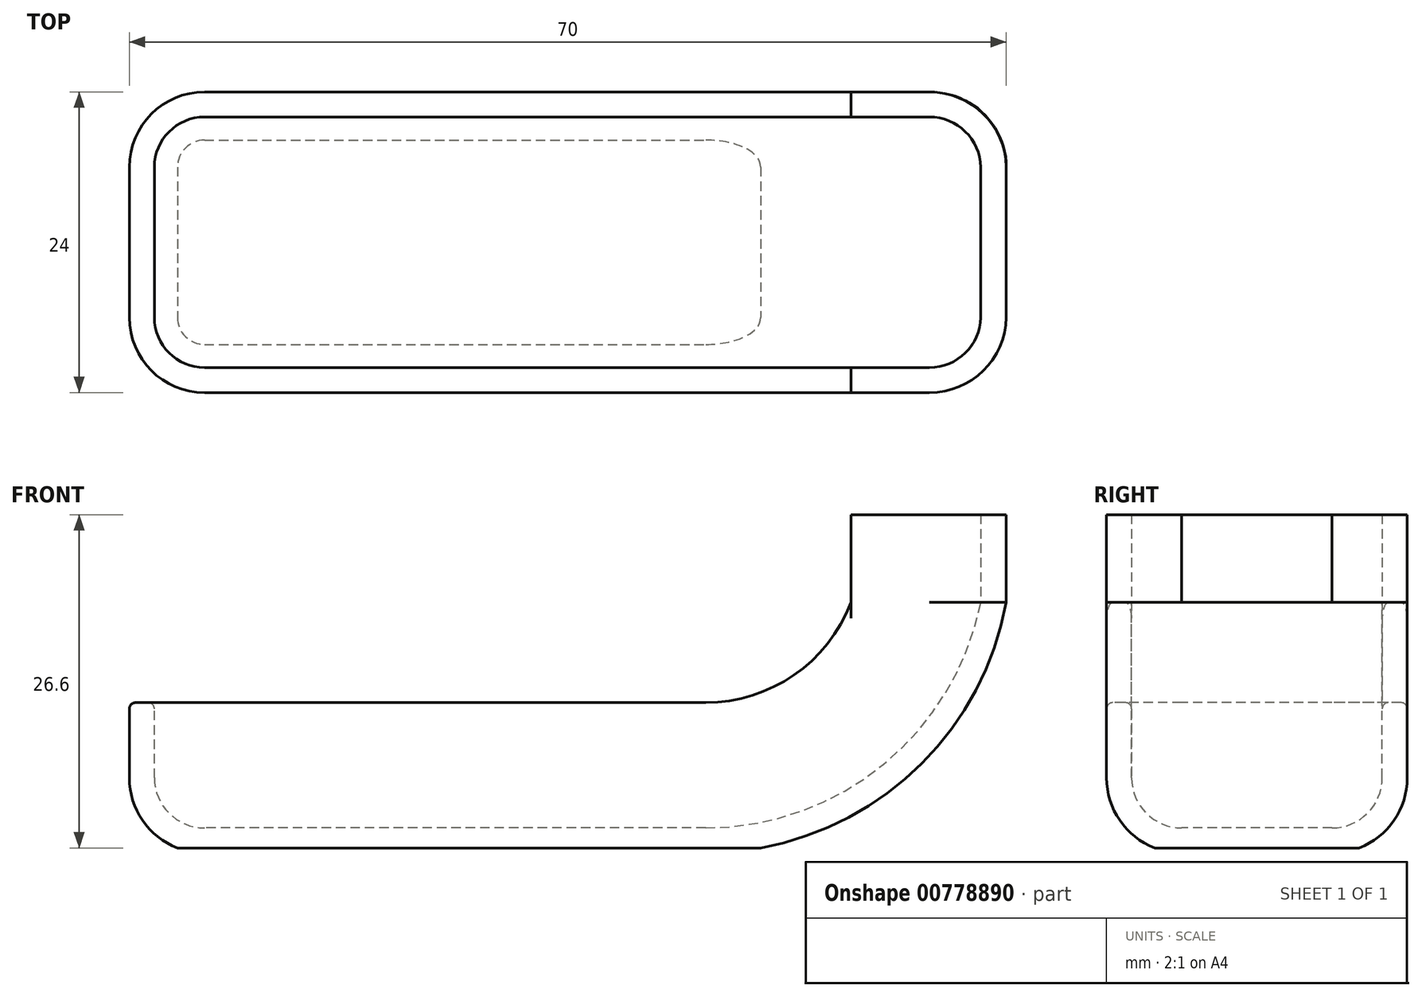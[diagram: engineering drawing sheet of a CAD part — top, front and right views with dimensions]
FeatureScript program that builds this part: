
annotation { "Feature Type Name" : "Feature", "Feature Type Description" : "" }
export const myFeature = defineFeature(function(context is Context, id is Id, definition is map)
    precondition{}
    {
        {
            var Q0;
            Q0=qCreatedBy(makeId("Front.planeOp"),FACE);
            var sketch = newSketch(context, id + "F0", { "sketchPlane" : qUnion([Q0])});
            skLineSegment(sketch, "E0", {"start": v(46, -24.4) * mm, "end": v(0, -24.4) * mm});
            skArc(sketch, "E1", {"start": v(46, -24.4) * mm, "mid": v(61.62, -18.74) * mm, "end": v(70, -4.4) * mm});
            skSolve(sketch);
        }
        {
            var Q0;
            Q0=qCreatedBy(makeId("Right.planeOp"),FACE);
            var sketch = newSketch(context, id + "F1", { "sketchPlane" : qUnion([Q0])});
            skArc(sketch, "E2", {"start": v(6, -24.4) * mm, "mid": v(10.24, -22.64) * mm, "end": v(12, -18.4) * mm});
            skArc(sketch, "E3", {"start": v(-12, -18.4) * mm, "mid": v(-10.24, -22.64) * mm, "end": v(-6, -24.4) * mm});
            skLineSegment(sketch, "E4", {"start": v(6, -24.4) * mm, "end": v(-6, -24.4) * mm});
            skLineSegment(sketch, "E5", {"start": v(12, -18.4) * mm, "end": v(12, -12.4) * mm});
            skLineSegment(sketch, "E6", {"start": v(12, -12.4) * mm, "end": v(-12, -12.4) * mm});
            skLineSegment(sketch, "E7", {"start": v(-12, -12.4) * mm, "end": v(-12, -18.4) * mm});
            skSolve(sketch);
        }
        {
            var Q0;
            Q0 = qSketchRegion(id + "F1", true);
            var Q1;
            Q1 = qConstructionFilter(qBodyType(qCreatedBy(id + "F0" ,EDGE), BodyType.WIRE), ConstructionObject.NO);
            sweep(context, id + "F2", {"profiles" : qUnion([Q0]), "path" : qUnion([Q1])});
        }
        {
            var Q0;
            Q0=makeQuery(id+"F2.opSweep","CAP_EDGE",EDGE,{"disambiguationData":[OSD([sQuery(id+"F0.wireOp",VERTEX,"E0.end"),sQuery(id+"F1.wireOp",EDGE,"E7")])],"isStart":true});
            fillet(context, id + "F3", {"entities" : qUnion([Q0]), "radius" : 6 * mm, "tangentPropagation" : true, "allowEdgeOverflow" : false});
        }
        {
            var Q0;
            Q0=makeQuery(id+"F2.opSweep","SWEPT_FACE",FACE,{"disambiguationData":[OSD([sQuery(id+"F0.wireOp",EDGE,"E0"),sQuery(id+"F1.wireOp",EDGE,"E6")])]});
            var Q1;
            Q1=makeQuery(id+"F2.opSweep","SWEPT_FACE",FACE,{"disambiguationData":[OSD([sQuery(id+"F0.wireOp",EDGE,"E1"),sQuery(id+"F1.wireOp",EDGE,"E6")])]});
            var Q2;
            Q2=makeQuery(id+"F2.opSweep","CAP_FACE",FACE,{"disambiguationData":[OSD([sQuery(id+"F0.wireOp",VERTEX,"E1.end"),sQuery(id+"F1.wireOp",EDGE,"E2"),sQuery(id+"F1.wireOp",EDGE,"E3"),sQuery(id+"F1.wireOp",EDGE,"E4"),sQuery(id+"F1.wireOp",EDGE,"E5"),sQuery(id+"F1.wireOp",EDGE,"E6"),sQuery(id+"F1.wireOp",EDGE,"E7")])],"isStart":false});
            shell(context, id + "F4", {"entities" : qUnion([Q0, Q1, Q2]), "thickness" : 2 * mm});
        }
        {
            var Q0;
            Q0=qCreatedBy(makeId("Top.planeOp"),FACE);
            var Q1;
            Q1=makeQuery(id+"F2.opSweep","CAP_VERTEX",VERTEX,{"disambiguationData":[OSD([sQuery(id+"F0.wireOp",EDGE,"E1"),sQuery(id+"F1.wireOp",EDGE,"E3"),sQuery(id+"F1.wireOp",EDGE,"E4")])],"isStart":false});
            cPlane(context, id + "F5", {"entities" : qUnion([Q0, Q1]), "cplaneType" : CPlaneType.PLANE_POINT, "offset" : 4 * mm, "oppositeDirection" : true, "width" : 150 * mm, "height" : 150 * mm});
        }
        {
            var Q0;
            Q0=qCreatedBy(id+"F5.planeOp",FACE);
            var sketch = newSketch(context, id + "F6", { "sketchPlane" : qUnion([Q0])});
            skLineSegment(sketch, "E8.bottom", {"start": v(34.96, 35.18) * mm, "end": v(78.53, 35.18) * mm});
            skLineSegment(sketch, "E8.top", {"start": v(34.96, -36.07) * mm, "end": v(78.53, -36.07) * mm});
            skLineSegment(sketch, "E8.left", {"start": v(34.96, 35.18) * mm, "end": v(34.96, -36.07) * mm});
            skLineSegment(sketch, "E8.right", {"start": v(78.53, 35.18) * mm, "end": v(78.53, -36.07) * mm});
            skSolve(sketch);
        }
        {
            var Q0;
            Q0 = qSketchRegion(id + "F6", true);
            extrude(context, id + "F7", {"entities" : qUnion([Q0]), "operationType" : NewBodyOperationType.REMOVE, "depth" : 25.2 * mm, "offsetDistance" : 25 * mm});
        }
        {
            var Q0;
            Q0=makeQuery(id+"F7.boolean.opBoolean","COPY",FACE,{"derivedFrom":makeQuery(id+"F7.opExtrude","CAP_FACE",FACE,{"disambiguationData":[OSD([sQuery(id+"F6.wireOp",EDGE,"E8.bottom"),sQuery(id+"F6.wireOp",EDGE,"E8.top"),sQuery(id+"F6.wireOp",EDGE,"E8.left"),sQuery(id+"F6.wireOp",EDGE,"E8.right")])],"isStart":true})});
            var sketch = newSketch(context, id + "F8", { "sketchPlane" : qUnion([Q0])});
            skLineSegment(sketch, "E9", {"start": v(57.6, 12) * mm, "end": v(57.6, 10) * mm});
            skLineSegment(sketch, "E10", {"start": v(57.6, 10) * mm, "end": v(63.87, 10) * mm});
            skLineSegment(sketch, "E11", {"start": v(57.6, -10) * mm, "end": v(63.87, -10) * mm});
            skLineSegment(sketch, "E12", {"start": v(57.6, -10) * mm, "end": v(57.6, -12) * mm});
            skLineSegment(sketch, "E13", {"start": v(57.6, -12) * mm, "end": v(63.87, -12) * mm});
            skLineSegment(sketch, "E14", {"start": v(67.96, -6) * mm, "end": v(67.96, 6) * mm});
            skLineSegment(sketch, "E15", {"start": v(70, 6) * mm, "end": v(70, -6) * mm});
            skLineSegment(sketch, "E16", {"start": v(57.6, 12) * mm, "end": v(63.87, 12) * mm});
            skArc(sketch, "E17", {"start": v(67.96, 6) * mm, "mid": v(66.73, 8.83) * mm, "end": v(63.87, 10) * mm});
            skArc(sketch, "E18", {"start": v(70, 6) * mm, "mid": v(68.16, 10.25) * mm, "end": v(63.87, 12) * mm});
            skArc(sketch, "E19", {"start": v(63.87, -10) * mm, "mid": v(66.73, -8.83) * mm, "end": v(67.96, -6) * mm});
            skArc(sketch, "E20", {"start": v(63.87, -12) * mm, "mid": v(68.16, -10.25) * mm, "end": v(70, -6) * mm});
            skSolve(sketch);
        }
        {
            var Q0;
            Q0 = qSketchRegion(id + "F8", true);
            extrude(context, id + "F9", {"entities" : qUnion([Q0]), "operationType" : NewBodyOperationType.ADD, "depth" : 7 * mm, "offsetDistance" : 25 * mm});
        }
        {
            var Q0;
            Q0=makeQuery(id+"F2.opSweep","CAP_FACE",FACE,{"disambiguationData":[OSD([sQuery(id+"F0.wireOp",VERTEX,"E0.end"),sQuery(id+"F1.wireOp",EDGE,"E2"),sQuery(id+"F1.wireOp",EDGE,"E3"),sQuery(id+"F1.wireOp",EDGE,"E4"),sQuery(id+"F1.wireOp",EDGE,"E5"),sQuery(id+"F1.wireOp",EDGE,"E6"),sQuery(id+"F1.wireOp",EDGE,"E7")])],"isStart":true});
            var sketch = newSketch(context, id + "F10", { "sketchPlane" : qUnion([Q0])});
            skLineSegment(sketch, "E21.bottom", {"start": v(-9.54, -29.35) * mm, "end": v(11.5, -29.35) * mm});
            skLineSegment(sketch, "E21.top", {"start": v(-9.54, -24) * mm, "end": v(11.5, -24) * mm});
            skLineSegment(sketch, "E21.left", {"start": v(-9.54, -29.35) * mm, "end": v(-9.54, -24) * mm});
            skLineSegment(sketch, "E21.right", {"start": v(11.5, -29.35) * mm, "end": v(11.5, -24) * mm});
            skSolve(sketch);
        }
        {
            var Q0;
            Q0=makeQuery(id+"F10.imprint","IMPRINT",FACE,{"disambiguationData":[TD([[makeQuery(id+"F10.imprint","IMPRINT",EDGE,{"derivedFrom":sQuery(id+"F10.wireOp",EDGE,"E21.bottom")}),1.0]])]});
            extrude(context, id + "F11", {"entities" : qUnion([Q0]), "operationType" : NewBodyOperationType.REMOVE, "oppositeDirection" : true, "depth" : 73.3 * mm, "offsetDistance" : 25 * mm});
        }
        {
            var Q0;
            Q0=makeQuery(id+"F2.opSweep","SWEPT_EDGE",EDGE,{"disambiguationData":[OSD([sQuery(id+"F0.wireOp",EDGE,"E0"),sQuery(id+"F1.wireOp",EDGE,"E6"),sQuery(id+"F1.wireOp",EDGE,"E7")])]});
            var Q1;
            Q1=makeQuery(id+"F4.opShell","OFFSET_EDGE",EDGE,{"disambiguationData":[OSD([sQuery(id+"F0.wireOp",VERTEX,"E0.end"),sQuery(id+"F1.wireOp",EDGE,"E6")])]});
            fillet(context, id + "F12", {"entities" : qUnion([Q0, Q1]), "radius" : 0.5 * mm, "tangentPropagation" : true, "allowEdgeOverflow" : false});
        }
    });
